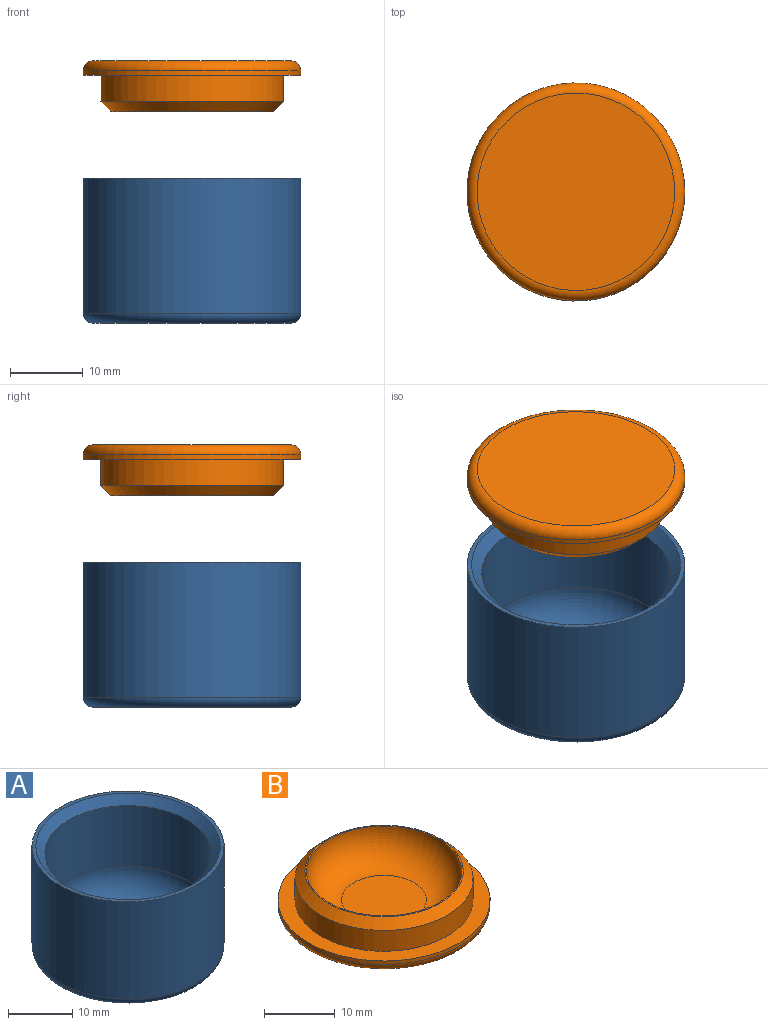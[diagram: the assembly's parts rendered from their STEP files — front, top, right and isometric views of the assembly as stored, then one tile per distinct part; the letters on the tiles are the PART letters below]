
ASSEMBLY  parts=2 mates=1
PART A: 8 faces, bbox 32.5x32.5x20 mm
  f0: cylinder r=15mm len=30mm, axis (0,0,-1), area 1753mm2, adj f3,f7
  f1: plane 27.2x27.2mm, normal (0,0,-1), area 581.1mm2, adj f7
  f2: cylinder r=13mm len=26mm, axis (0,0,-1), area 947.5mm2, adj f5,f6
  f3: plane 30x30mm, normal (0,0,1), area 55.4mm2, adj f0,f6
  f4: plane 16x16mm, normal (0,0,1), area 201.1mm2, adj f5
  f5: torus R=8mm, axis (0,0,1), area 551.9mm2, adj f2,f4
  f6: cone r=13mm half-angle=45deg, axis (0,0,1), area 170.4mm2, adj f2,f3
  f7: torus R=13.6mm, axis (0,0,1), area 200.2mm2, adj f0,f1
PART B: 9 faces, bbox 32.5x32.5x10.6 mm
  f0: cylinder r=15mm len=30mm, axis (0,0,-1), area 56.5mm2, adj f1,f8
  f1: plane 30x30mm, normal (0,0,1), area 208.1mm2, adj f0,f3
  f2: plane 27.2x27.2mm, normal (0,0,-1), area 581.1mm2, adj f8
  f3: cylinder r=12.6mm len=25.2mm, axis (0,0,-1), area 285mm2, adj f1,f7
  f4: plane 22.4x22.4mm, normal (0,0,1), area 13.9mm2, adj f6,f7
  f5: plane 12x12mm, normal (0,0,1), area 113.1mm2, adj f6
  f6: torus R=6mm, axis (0,0,1), area 453.2mm2, adj f4,f5
  f7: cone r=11.2mm half-angle=45deg, axis (0,0,-1), area 148mm2, adj f3,f4
  f8: torus R=13.6mm, axis (0,0,1), area 200.2mm2, adj f0,f2
PLACE A t=(5.61,3.32,-22.45)mm
PLACE B rot(axis=(1,0,0),180deg) t=(5.61,3.32,13.71)mm
MATE cylindrical B.f0 <-> A.f0  axis (0,0,1) through (5.61,3.32,11.71)mm
